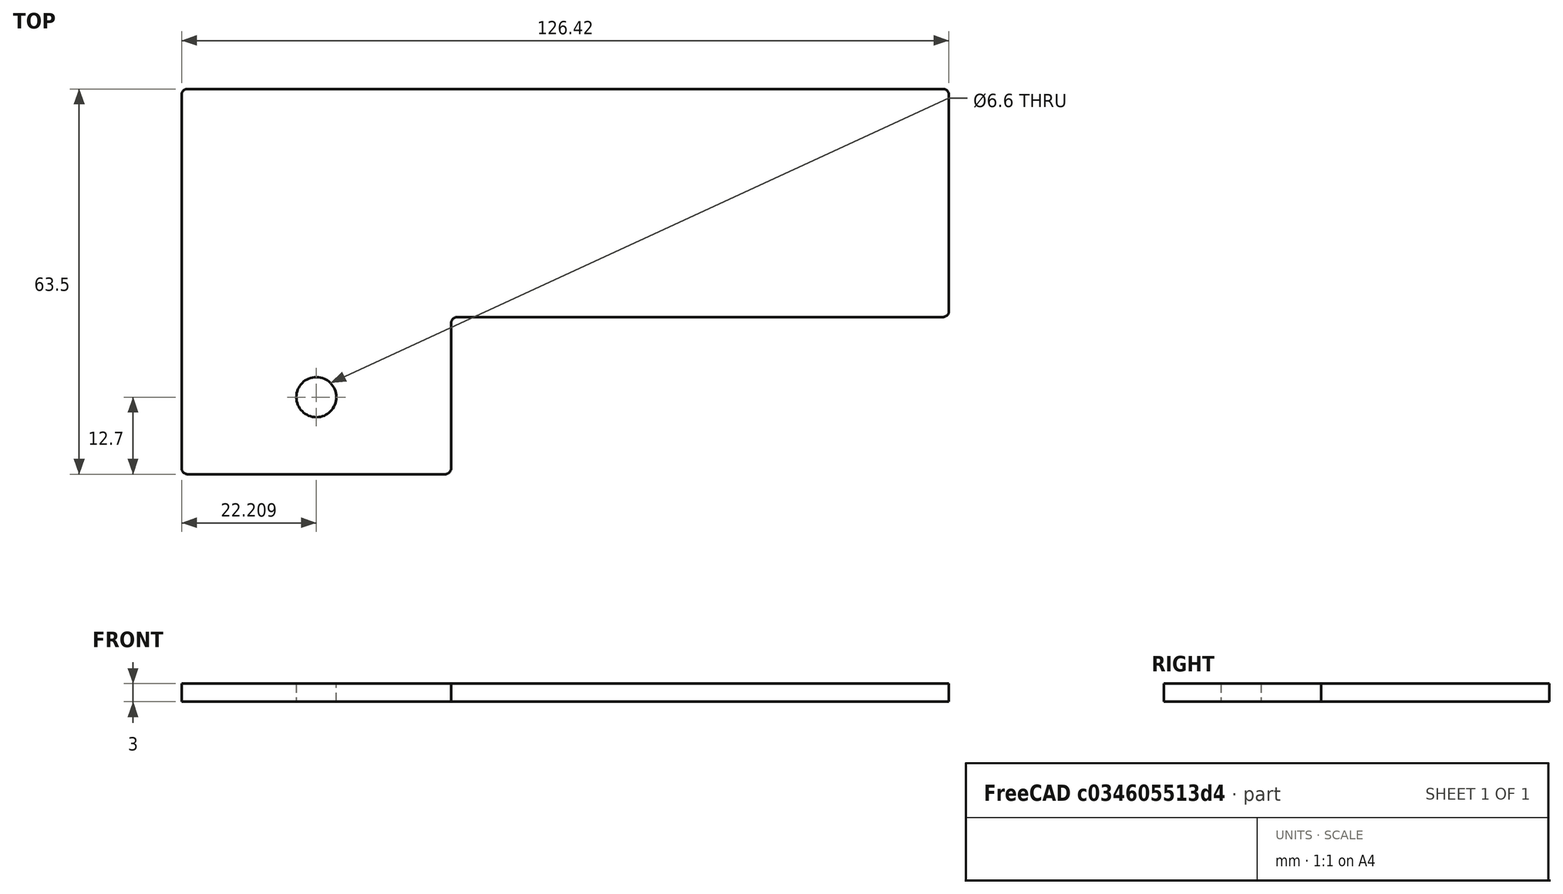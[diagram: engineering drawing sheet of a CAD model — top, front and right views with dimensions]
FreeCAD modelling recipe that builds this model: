
FCSTD DOCUMENT  (FreeCAD 0.20R29603 (Git))
Label: right_wall_front_test_rig
License: All rights reserved
LicenseURL: http://en.wikipedia.org/wiki/All_rights_reserved
objects: Sketcher::SketchObject×2, Spreadsheet::Sheet×1, PartDesign::Pad×1, PartDesign::Body×1, Part::Part2DObjectPython×1
note: 6 computed .brp shape members not serialized (recipe doc carries the construction recipe); baked Part::Feature solids carry a one-line shape summary decoded from their .brp

FEATURE [Spreadsheet::Sheet] Spreadsheet
  cells = A2=Parameters; A3=BeamLength; B3(BeamLength)==7.8125in; A4=BracketLength; B4(BracketLength)==108.6mm; A5=DistanceLeftBracketEdgeToDoor; B5(DistanceLeftBracketEdgeToDoor)==82.4999mm; A6=DistanceRightBracketEdgeToDoor; B6(DistanceRightBracketEdgeToDoor)==23.6001mm; A7=LengthMargin; B7(LengthMargin)==0.5mm; A8=LengthLeftBracketEdgeToDoorGap; B8(LengthLeftBracketEdgeToDoorGap)==DistanceLeftBracketEdgeToDoor - LengthMargin; A9=LengthRightBracketEdgeToDoorGap; B9(LengthRightBracketEdgeToDoorGap)==DistanceRightBracketEdgeToDoor - LengthMargin; A10=LengthDoorGap; B10(LengthDoorGap)==BracketLength - LengthLeftBracketEdgeToDoorGap - LengthRightBracketEdgeToDoorGap; A11=BeamLengthMinusBracketLength; B11(BeamLengthMinusBracketLength)==BeamLength - BracketLength; A12=DistanceFrontToDoor; B12(DistanceFrontToDoor)==0.5 * BeamLengthMinusBracketLength + LengthLeftBracketEdgeToDoorGap; A13=DistanceFrontToBracket; B13(DistanceFrontToBracket)==0.5 * BeamLengthMinusBracketLength; A14=LengthFrontToDoor; B14(LengthFrontToDoor)==DistanceFrontToDoor - LengthMargin; A15=LengthFrontToBracket; B15(LengthFrontToBracket)==DistanceFrontToBracket - LengthMargin; A16=Height; B16(Height)==2.5in; A17=Thickness; B17(Thickness)==3mm; A18=CutoutMargin; B18(CutoutMargin)==0.5mm; A19=CutoutHeight; B19(CutoutHeight)==1in + CutoutMargin; A20=FilletRadius; B20(FilletRadius)==1mm; A21=MountHoleDiameter; B21(MountHoleDiameter)==0.26in; A22=MountHoleDistanceFromBottom; B22(MountHoleDistanceFromBottom)==0.5in
FEATURE [Sketcher::SketchObject] Sketch
  FullyConstrained = true
  MapMode = 5
  Support = -> [XY_Plane]
  expr: Constraints[14] = Spreadsheet.FilletRadius
  expr: Constraints[20] = Spreadsheet.Height
  expr: Constraints[43] = Spreadsheet.MountHoleDistanceFromBottom
  expr: Constraints[44] = Spreadsheet.MountHoleDiameter
  expr: Constraints[7] = Spreadsheet.LengthFrontToDoor
  expr: Constraints[8] = Spreadsheet.LengthFrontToBracket
  expr: Constraints[9] = Spreadsheet.CutoutHeight
  sketch-geometry (21):
    g0: LineSegment StartX=0 StartY=62.5 StartZ=0 EndX=0 EndY=1 EndZ=0
    g1: LineSegment StartX=1 StartY=0 StartZ=0 EndX=43.4188 EndY=0 EndZ=0
    g2: LineSegment StartX=44.4188 StartY=1 StartZ=0 EndX=44.4188 EndY=24.9 EndZ=0
    g3: LineSegment StartX=45.4188 StartY=25.9 StartZ=0 EndX=125.419 EndY=25.9 EndZ=0
    g4: LineSegment StartX=126.419 StartY=26.9 StartZ=0 EndX=126.419 EndY=62.5 EndZ=0
    g5: LineSegment StartX=125.419 StartY=63.5 StartZ=0 EndX=1 EndY=63.5 EndZ=0
    g6: ArcOfCircle CenterX=1 CenterY=62.5 CenterZ=0 NormalX=0 NormalY=0 NormalZ=1 AngleXU=0 Radius=1 StartAngle=1.5708 EndAngle=3.14159
    g7: GeomPoint X=0 Y=63.5 Z=0
    g8: ArcOfCircle CenterX=1 CenterY=1 CenterZ=0 NormalX=0 NormalY=0 NormalZ=1 AngleXU=0 Radius=1 StartAngle=3.14159 EndAngle=4.71239
    g9: GeomPoint X=0 Y=0 Z=0
    g10: ArcOfCircle CenterX=43.4188 CenterY=1 CenterZ=0 NormalX=0 NormalY=0 NormalZ=1 AngleXU=0 Radius=1 StartAngle=4.71239 EndAngle=6.28319
    g11: GeomPoint X=44.4188 Y=0 Z=0
    g12: ArcOfCircle CenterX=45.4188 CenterY=24.9 CenterZ=0 NormalX=0 NormalY=0 NormalZ=1 AngleXU=0 Radius=1 StartAngle=1.5708 EndAngle=3.14159
    g13: GeomPoint X=44.4188 Y=25.9 Z=0
    g14: ArcOfCircle CenterX=125.419 CenterY=26.9 CenterZ=0 NormalX=0 NormalY=0 NormalZ=1 AngleXU=0 Radius=1 StartAngle=4.71239 EndAngle=6.28319
    g15: GeomPoint X=126.419 Y=25.9 Z=0
    g16: ArcOfCircle CenterX=125.419 CenterY=62.5 CenterZ=0 NormalX=0 NormalY=0 NormalZ=1 AngleXU=0 Radius=1 StartAngle=3.5e-15 EndAngle=1.5708
    g17: GeomPoint X=126.419 Y=63.5 Z=0
    g18: GeomPoint X=22.2094 Y=0 Z=0
    g19: LineSegment StartX=22.2094 StartY=0 StartZ=0 EndX=22.2094 EndY=12.7 EndZ=0
    g20: Circle CenterX=22.2094 CenterY=12.7 CenterZ=0 NormalX=0 NormalY=0 NormalZ=1 AngleXU=0 Radius=3.302
  constraints (47):
    c: Vertical(g0)
    c: Horizontal(g1)
    c: Vertical(g2)
    c: Horizontal(g3)
    c: Vertical(g4)
    c: Horizontal(g5)
    c: Coincident(g-1,g9)
    c: DistanceX(g7,g17) = 126.419
    c: DistanceX(g9,g11) = 44.4188
    c: DistanceY(g11,g13) = 25.9
    c: PointOnObject(g7,g0)
    c: PointOnObject(g7,g5)
    c: Tangent(g0,g6) = -1.5708
    c: Tangent(g5,g6) = -1.5708
    c: Radius(g6) = 1
    c: PointOnObject(g9,g0)
    c: PointOnObject(g9,g1)
    c: Tangent(g0,g8) = -1.5708
    c: Tangent(g1,g8) = -1.5708
    c: Equal(g8,g6)
    c: DistanceY(g1,g5) = 63.5
    c: PointOnObject(g11,g1)
    c: PointOnObject(g11,g2)
    c: Tangent(g1,g10) = -1.5708
    c: Tangent(g2,g10) = -1.5708
    c: Equal(g10,g8)
    c: PointOnObject(g13,g2)
    c: PointOnObject(g13,g3)
    c: Tangent(g2,g12) = 1.5708
    c: Tangent(g3,g12) = 1.5708
    c: Equal(g12,g10)
    c: PointOnObject(g15,g3)
    c: PointOnObject(g15,g4)
    c: Tangent(g3,g14) = -1.5708
    c: Tangent(g4,g14) = -1.5708
    c: Equal(g14,g12)
    c: PointOnObject(g17,g5)
    c: PointOnObject(g17,g4)
    c: Tangent(g5,g16) = -1.5708
    c: Tangent(g4,g16) = -1.5708
    c: Equal(g16,g14)
    c: Coincident(g19,g18)
    c: Vertical(g19)
    c: DistanceY(g19,g19) = 12.7
    c: Diameter(g20) = 6.604
    c: Coincident(g19,g20)
    c: Symmetric(g1,g1,g18)
FEATURE [PartDesign::Pad] Pad
  Direction = (0,0,1)
  Length = 3
  Length2 = 10
  Profile = -> Sketch
  ReferenceAxis = -> Sketch [N_Axis]
  Type = 0
  expr: Length = Spreadsheet.Thickness
FEATURE [PartDesign::Body] Body
  Group = -> [Sketch,Pad]
  Origin = -> Origin
  Tip = -> Pad
FEATURE [Part::Part2DObjectPython] Shape2DView  # Draft 2D object (typed FeaturePython)
  AutoUpdate = true
  Base = -> Pad
  Clip = false
  FaceNumbers = [14]
  FuseArch = false
  HiddenLines = false
  InPlace = true
  OnlySolids = false
  Projection = (0,0,1)
  ProjectionMode = 0
  SegmentLength = 0.05
  Tessellation = false
  VisibleOnly = false
FEATURE [Sketcher::SketchObject] Sketch001
  FullyConstrained = false
  sketch-geometry (13):
    g0: LineSegment StartX=45.4188 StartY=25.9 StartZ=0 EndX=125.419 EndY=25.9 EndZ=0
    g1: ArcOfCircle CenterX=125.419 CenterY=26.9 CenterZ=0 NormalX=0 NormalY=0 NormalZ=1 AngleXU=0 Radius=1 StartAngle=4.71239 EndAngle=6.28319
    g2: LineSegment StartX=126.419 StartY=26.9 StartZ=0 EndX=126.419 EndY=62.5 EndZ=0
    g3: ArcOfCircle CenterX=125.419 CenterY=62.5 CenterZ=0 NormalX=0 NormalY=0 NormalZ=1 AngleXU=0 Radius=1 StartAngle=4e-15 EndAngle=1.5708
    g4: LineSegment StartX=125.419 StartY=63.5 StartZ=0 EndX=1 EndY=63.5 EndZ=0
    g5: ArcOfCircle CenterX=1 CenterY=62.5 CenterZ=0 NormalX=0 NormalY=0 NormalZ=1 AngleXU=0 Radius=1 StartAngle=1.5708 EndAngle=3.14159
    g6: LineSegment StartX=0 StartY=62.5 StartZ=0 EndX=0 EndY=1 EndZ=0
    g7: ArcOfCircle CenterX=1 CenterY=1 CenterZ=0 NormalX=0 NormalY=0 NormalZ=1 AngleXU=0 Radius=1 StartAngle=3.14159 EndAngle=4.71239
    g8: LineSegment StartX=1 StartY=0 StartZ=0 EndX=43.4188 EndY=0 EndZ=0
    g9: ArcOfCircle CenterX=43.4188 CenterY=1 CenterZ=0 NormalX=0 NormalY=0 NormalZ=1 AngleXU=0 Radius=1 StartAngle=4.71239 EndAngle=6.28319
    g10: LineSegment StartX=44.4188 StartY=1 StartZ=0 EndX=44.4188 EndY=24.9 EndZ=0
    g11: ArcOfCircle CenterX=45.4188 CenterY=24.9 CenterZ=0 NormalX=0 NormalY=0 NormalZ=1 AngleXU=0 Radius=1 StartAngle=1.5708 EndAngle=3.14159
    g12: Circle CenterX=22.2094 CenterY=12.7 CenterZ=0 NormalX=0 NormalY=0 NormalZ=1 AngleXU=0 Radius=3.302
